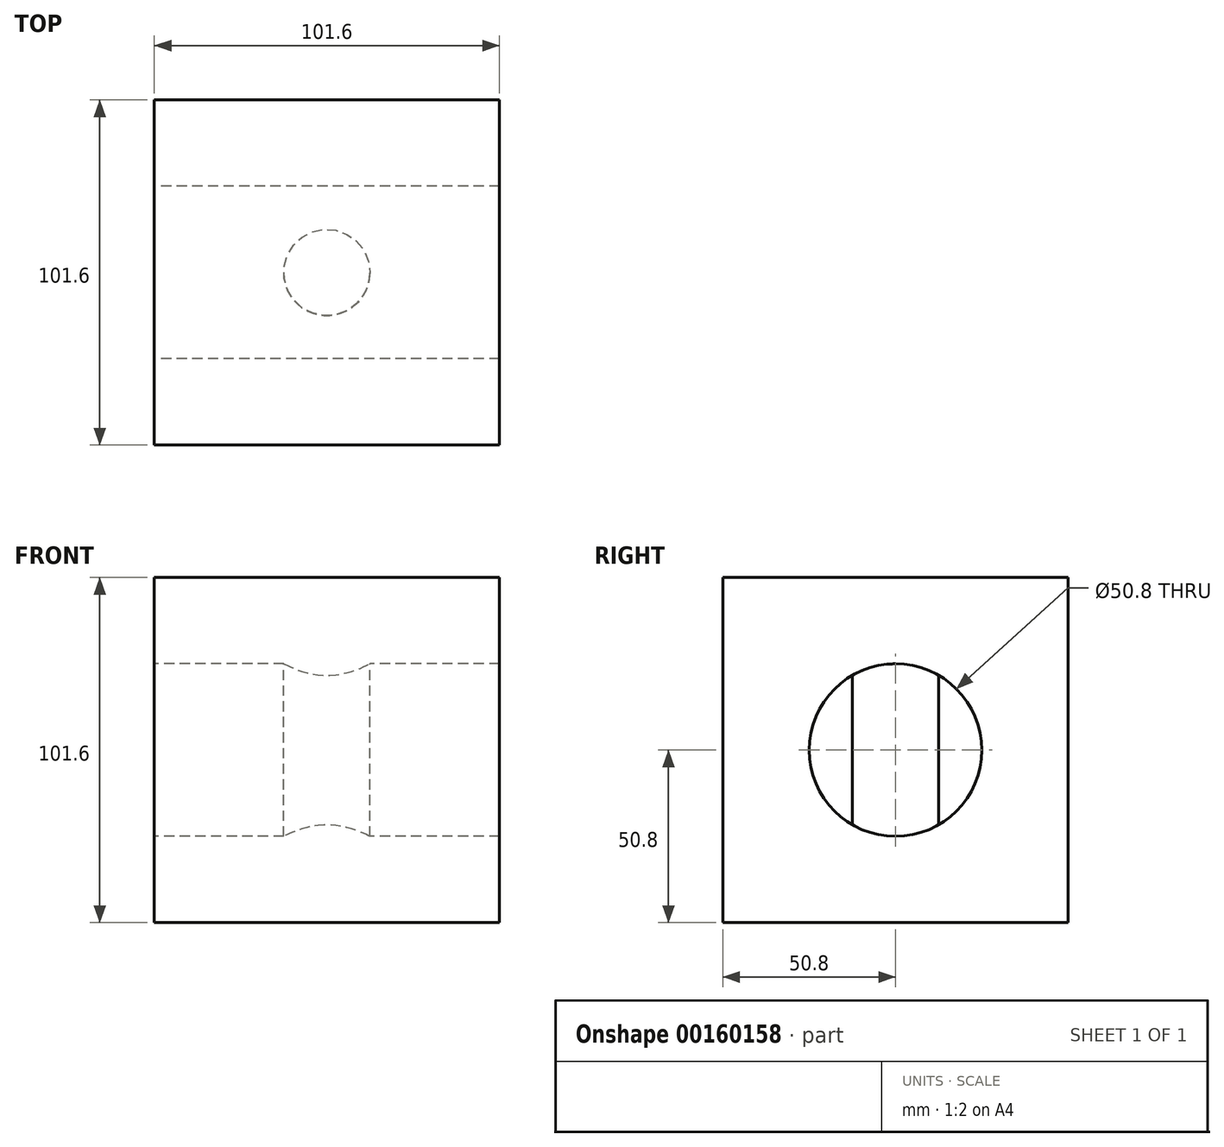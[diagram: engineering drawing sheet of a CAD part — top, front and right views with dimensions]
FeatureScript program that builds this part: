
annotation { "Feature Type Name" : "Feature", "Feature Type Description" : "" }
export const myFeature = defineFeature(function(context is Context, id is Id, definition is map)
    precondition{}
    {
        {
            var Q0;
            Q0=qCreatedBy(makeId("Front.planeOp"),FACE);
            var sketch = newSketch(context, id + "F3", { "sketchPlane" : qUnion([Q0])});
            skLineSegment(sketch, "E0.bottom", {"start": v(50.8, 50.8) * mm, "end": v(-50.8, 50.8) * mm});
            skLineSegment(sketch, "E0.top", {"start": v(50.8, -50.8) * mm, "end": v(-50.8, -50.8) * mm});
            skLineSegment(sketch, "E0.left", {"start": v(50.8, 50.8) * mm, "end": v(50.8, -50.8) * mm});
            skLineSegment(sketch, "E0.right", {"start": v(-50.8, 50.8) * mm, "end": v(-50.8, -50.8) * mm});
            skPoint(sketch, "E0.middle", {"position": v(0, 0) * mm});
            skSolve(sketch);
        }
        {
            var Q0;
            Q0 = qSketchRegion(id + "F3", true);
            extrude(context, id + "F4", {"entities" : qUnion([Q0]), "endBound" : BoundingType.SYMMETRIC, "depth" : 101.6 * mm});
        }
        {
            var Q0;
            Q0=makeQuery(id+"F4.opExtrude","SWEPT_FACE",FACE,{"disambiguationData":[OSD([sQuery(id+"F3.wireOp",EDGE,"E0.right")])]});
            var sketch = newSketch(context, id + "F0", { "sketchPlane" : qUnion([Q0])});
            skCircle(sketch, "E1", {"center": v(0, 0) * mm, "radius": 25.4 * mm});
            skSolve(sketch);
        }
        {
            var Q0;
            Q0 = qSketchRegion(id + "F0", true);
            extrude(context, id + "F5", {"entities" : qUnion([Q0]), "operationType" : NewBodyOperationType.REMOVE, "endBound" : BoundingType.THROUGH_ALL, "oppositeDirection" : true, "depth" : 25.4 * mm});
        }
        {
            var Q0;
            Q0=makeQuery(id+"F4.opExtrude","SWEPT_FACE",FACE,{"disambiguationData":[OSD([sQuery(id+"F3.wireOp",EDGE,"E0.bottom")])]});
            var sketch = newSketch(context, id + "F1", { "sketchPlane" : qUnion([Q0])});
            skCircle(sketch, "E2", {"center": v(0, 0) * mm, "radius": 12.7 * mm});
            skSolve(sketch);
        }
        {
            var Q0;
            Q0 = qSketchRegion(id + "F1", true);
            extrude(context, id + "F2", {"entities" : qUnion([Q0]), "operationType" : NewBodyOperationType.ADD, "oppositeDirection" : true, "depth" : 101.6 * mm});
        }
    });
